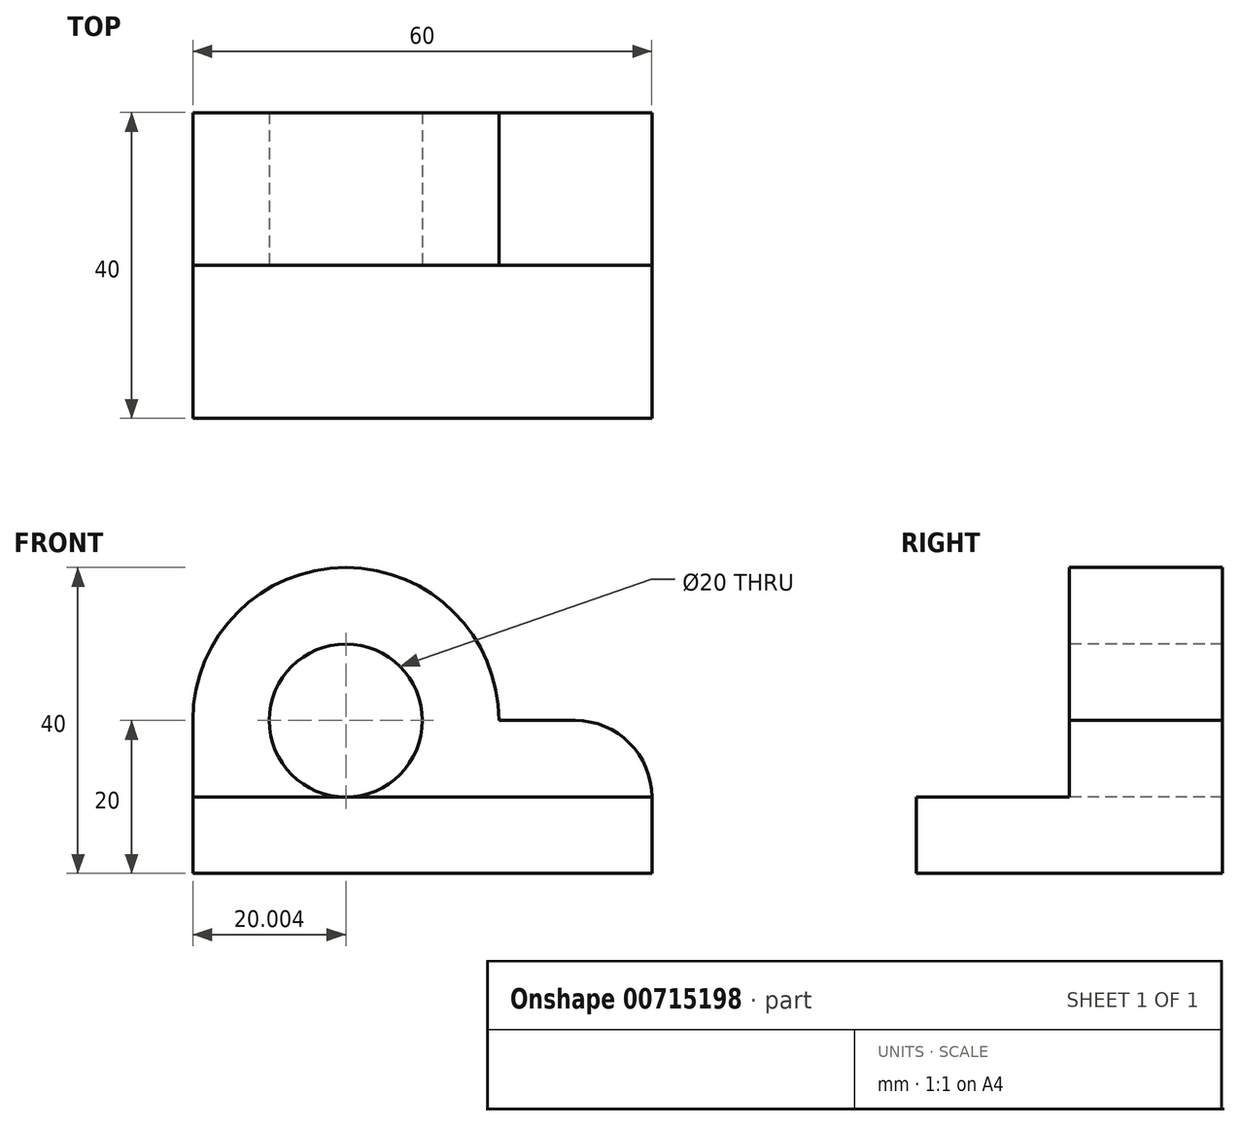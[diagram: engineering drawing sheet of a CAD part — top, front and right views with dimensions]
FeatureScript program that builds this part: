
annotation { "Feature Type Name" : "Feature", "Feature Type Description" : "" }
export const myFeature = defineFeature(function(context is Context, id is Id, definition is map)
    precondition{}
    {
        {
            var Q0;
            Q0=qCreatedBy(makeId("Top.planeOp"),FACE);
            var sketch = newSketch(context, id + "F0", { "sketchPlane" : qUnion([Q0])});
            skLineSegment(sketch, "E0.bottom", {"start": v(-27.33, 29.04) * mm, "end": v(32.67, 29.04) * mm});
            skLineSegment(sketch, "E0.top", {"start": v(-27.33, -10.96) * mm, "end": v(32.67, -10.96) * mm});
            skLineSegment(sketch, "E0.left", {"start": v(-27.33, 29.04) * mm, "end": v(-27.33, -10.96) * mm});
            skLineSegment(sketch, "E0.right", {"start": v(32.67, 29.04) * mm, "end": v(32.67, -10.96) * mm});
            skSolve(sketch);
        }
        {
            var Q0;
            Q0 = qSketchRegion(id + "F0", true);
            extrude(context, id + "F1", {"entities" : qUnion([Q0]), "depth" : 10 * mm, "offsetDistance" : 25.4 * mm});
        }
        {
            var Q0;
            Q0=makeQuery(id+"F1.opExtrude","CAP_FACE",FACE,{"disambiguationData":[OSD([sQuery(id+"F0.wireOp",EDGE,"E0.bottom"),sQuery(id+"F0.wireOp",EDGE,"E0.top"),sQuery(id+"F0.wireOp",EDGE,"E0.left"),sQuery(id+"F0.wireOp",EDGE,"E0.right")])],"isStart":false});
            var sketch = newSketch(context, id + "F2", { "sketchPlane" : qUnion([Q0])});
            skLineSegment(sketch, "E1.bottom", {"start": v(-27.33, 9.04) * mm, "end": v(32.67, 9.04) * mm});
            skLineSegment(sketch, "E1.top", {"start": v(-27.33, 29.04) * mm, "end": v(32.67, 29.04) * mm});
            skLineSegment(sketch, "E1.left", {"start": v(-27.33, 9.04) * mm, "end": v(-27.33, 29.04) * mm});
            skLineSegment(sketch, "E1.right", {"start": v(32.67, 9.04) * mm, "end": v(32.67, 29.04) * mm});
            skSolve(sketch);
        }
        {
            var Q0;
            Q0=makeQuery(id+"F2.imprint","IMPRINT",FACE,{"disambiguationData":[TD([[makeQuery(id+"F2.imprint","IMPRINT",EDGE,{"derivedFrom":sQuery(id+"F2.wireOp",EDGE,"E1.bottom")}),1.0]])]});
            extrude(context, id + "F3", {"entities" : qUnion([Q0]), "operationType" : NewBodyOperationType.ADD, "depth" : 10 * mm, "offsetDistance" : 25.4 * mm});
        }
        {
            var Q0;
            Q0=makeQuery(id+"F3.opExtrude","CAP_EDGE",EDGE,{"disambiguationData":[OSD([sQuery(id+"F2.wireOp",EDGE,"E1.right")])],"isStart":false});
            fillet(context, id + "F4", {"entities" : qUnion([Q0]), "radius" : 10 * mm, "tangentPropagation" : true, "allowEdgeOverflow" : false});
        }
        {
            var Q0;
            Q0=makeQuery(id+"F3.opExtrude","CAP_FACE",FACE,{"disambiguationData":[OSD([sQuery(id+"F2.wireOp",EDGE,"E1.bottom"),sQuery(id+"F2.wireOp",EDGE,"E1.top"),sQuery(id+"F2.wireOp",EDGE,"E1.left"),sQuery(id+"F2.wireOp",EDGE,"E1.right")])],"isStart":false});
            var sketch = newSketch(context, id + "F5", { "sketchPlane" : qUnion([Q0])});
            skLineSegment(sketch, "E2.bottom", {"start": v(-27.33, 29.04) * mm, "end": v(12.67, 29.04) * mm});
            skLineSegment(sketch, "E2.top", {"start": v(-27.33, 9.04) * mm, "end": v(12.67, 9.04) * mm});
            skLineSegment(sketch, "E2.left", {"start": v(-27.33, 29.04) * mm, "end": v(-27.33, 9.04) * mm});
            skLineSegment(sketch, "E2.right", {"start": v(12.67, 29.04) * mm, "end": v(12.67, 9.04) * mm});
            skSolve(sketch);
        }
        {
            var Q0;
            Q0=makeQuery(id+"F5.imprint","IMPRINT",FACE,{"disambiguationData":[TD([[makeQuery(id+"F5.imprint","IMPRINT",EDGE,{"derivedFrom":sQuery(id+"F5.wireOp",EDGE,"E2.bottom")}),-1.0]])]});
            extrude(context, id + "F6", {"entities" : qUnion([Q0]), "operationType" : NewBodyOperationType.ADD, "depth" : 20 * mm, "offsetDistance" : 25.4 * mm});
        }
        {
            var Q0;
            Q0=makeQuery(id+"F6.boolean.opBoolean","MERGE",FACE,{"derivedFrom":[makeQuery(id+"F3.opExtrude","SWEPT_FACE",FACE,{"disambiguationData":[OSD([sQuery(id+"F2.wireOp",EDGE,"E1.bottom")])]}),makeQuery(id+"F6.opExtrude","SWEPT_FACE",FACE,{"disambiguationData":[OSD([sQuery(id+"F5.wireOp",EDGE,"E2.top")])]})]});
            var sketch = newSketch(context, id + "F7", { "sketchPlane" : qUnion([Q0])});
            skLineSegment(sketch, "E3", {"start": v(-27.33, 10) * mm, "end": v(-27.33, 20) * mm});
            skCircle(sketch, "E4", {"center": v(-7.33, 20) * mm, "radius": 10 * mm});
            skPoint(sketch, "E4.centerSnap0", {"position": v(-7.33, 40) * mm});
            skSolve(sketch);
        }
        {
            var Q0;
            Q0=makeQuery(id+"F7.imprint","IMPRINT",FACE,{"disambiguationData":[TD([[makeQuery(id+"F7.imprint","IMPRINT",EDGE,{"derivedFrom":sQuery(id+"F7.wireOp",EDGE,"E4")}),1.0]])]});
            extrude(context, id + "F8", {"entities" : qUnion([Q0]), "operationType" : NewBodyOperationType.REMOVE, "oppositeDirection" : true, "depth" : 20 * mm, "offsetDistance" : 25.4 * mm});
        }
        {
            var Q0;
            Q0=makeQuery(id+"F6.opExtrude","CAP_EDGE",EDGE,{"disambiguationData":[OSD([sQuery(id+"F5.wireOp",EDGE,"E2.left")])],"isStart":false});
            var Q1;
            Q1=makeQuery(id+"F6.opExtrude","CAP_EDGE",EDGE,{"disambiguationData":[OSD([sQuery(id+"F5.wireOp",EDGE,"E2.right")])],"isStart":false});
            fillet(context, id + "F9", {"entities" : qUnion([Q0, Q1]), "radius" : 20 * mm, "tangentPropagation" : true, "allowEdgeOverflow" : false});
        }
    });
